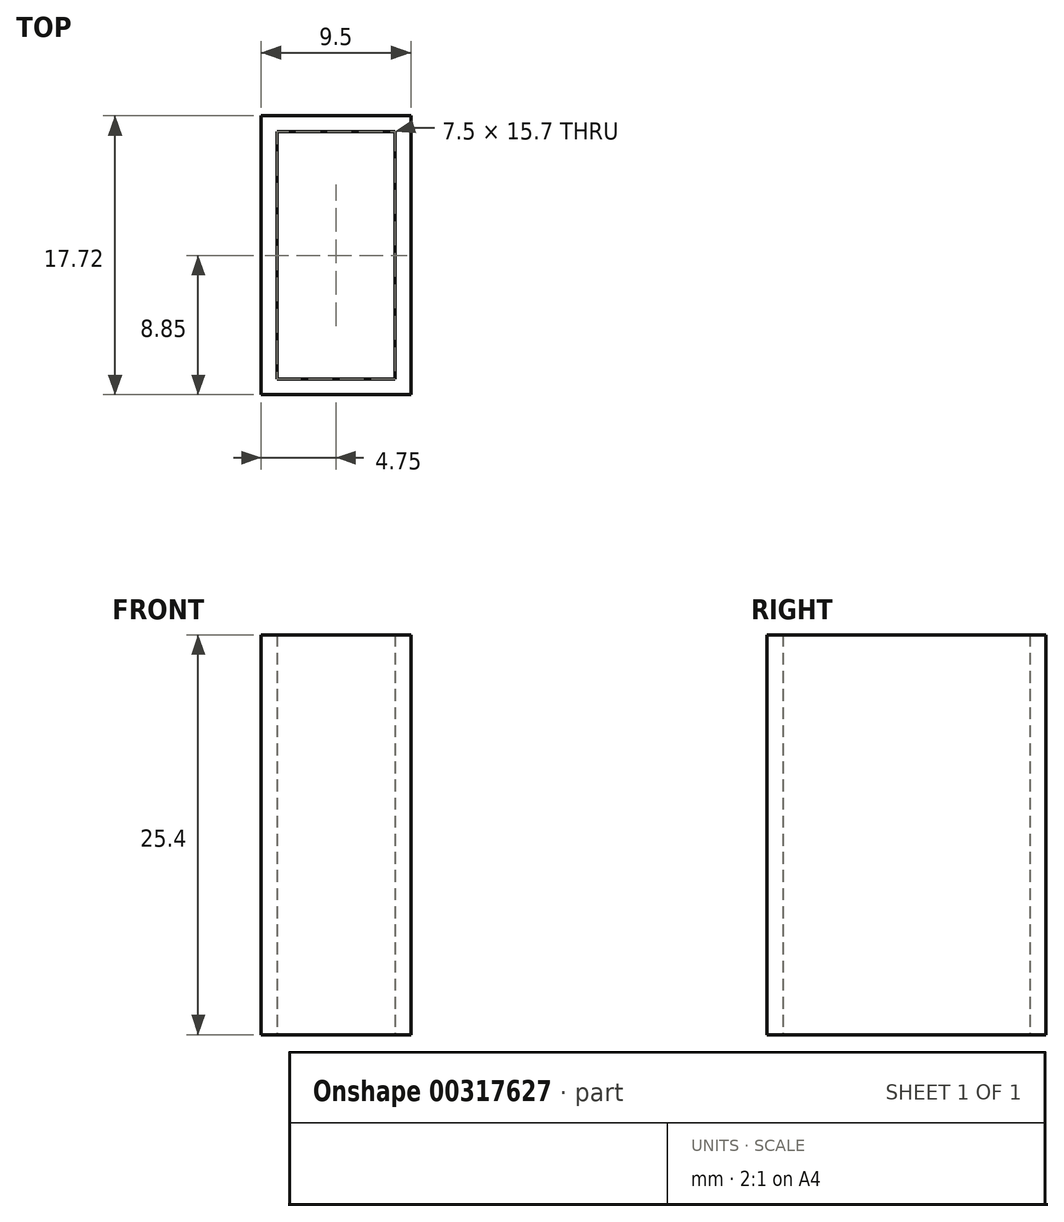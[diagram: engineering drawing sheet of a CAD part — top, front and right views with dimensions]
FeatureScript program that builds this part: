
annotation { "Feature Type Name" : "Feature", "Feature Type Description" : "" }
export const myFeature = defineFeature(function(context is Context, id is Id, definition is map)
    precondition{}
    {
        {
            var Q0;
            Q0=qCreatedBy(makeId("Top.planeOp"),FACE);
            var sketch = newSketch(context, id + "F0", { "sketchPlane" : qUnion([Q0])});
            skLineSegment(sketch, "E0.bottom", {"start": v(0, 0) * mm, "end": v(9.5, 0) * mm});
            skLineSegment(sketch, "E0.top", {"start": v(0, 17.72) * mm, "end": v(9.5, 17.72) * mm});
            skLineSegment(sketch, "E0.left", {"start": v(0, 0) * mm, "end": v(0, 17.72) * mm});
            skLineSegment(sketch, "E0.right", {"start": v(9.5, 0) * mm, "end": v(9.5, 17.72) * mm});
            skLineSegment(sketch, "E1.bottom", {"start": v(1, 16.7) * mm, "end": v(8.5, 16.7) * mm});
            skLineSegment(sketch, "E1.top", {"start": v(1, 1) * mm, "end": v(8.5, 1) * mm});
            skLineSegment(sketch, "E1.left", {"start": v(1, 16.7) * mm, "end": v(1, 1) * mm});
            skLineSegment(sketch, "E1.right", {"start": v(8.5, 16.7) * mm, "end": v(8.5, 1) * mm});
            skSolve(sketch);
        }
        {
            var Q0;
            Q0 = qSketchRegion(id + "F0", true);
            extrude(context, id + "F1", {"entities" : qUnion([Q0]), "depth" : 25.4 * mm});
        }
    });
